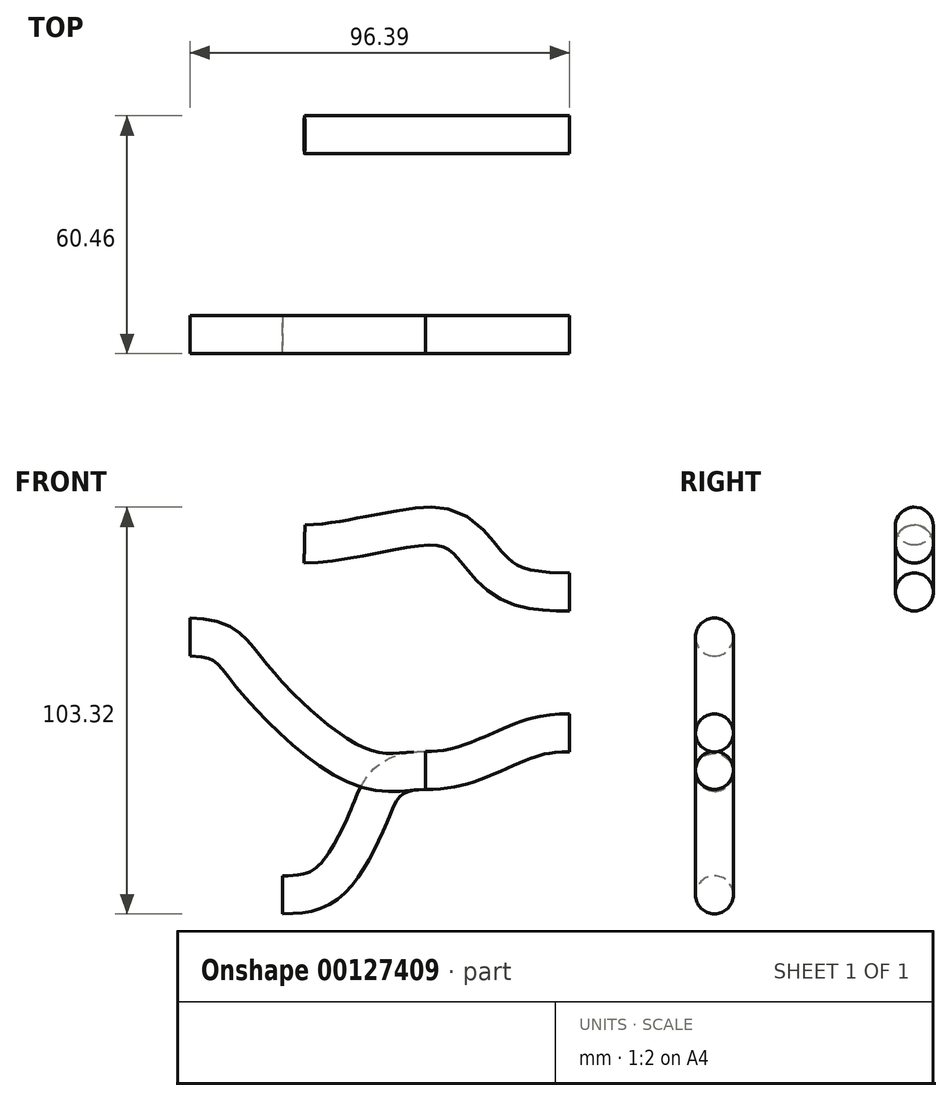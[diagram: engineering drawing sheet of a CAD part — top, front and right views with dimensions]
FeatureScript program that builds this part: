
annotation { "Feature Type Name" : "Feature", "Feature Type Description" : "" }
export const myFeature = defineFeature(function(context is Context, id is Id, definition is map)
    precondition{}
    {
        {
            var Q0;
            Q0=qCreatedBy(makeId("Front.planeOp"),FACE);
            var sketch = newSketch(context, id + "F0", { "sketchPlane" : qUnion([Q0])});
            skFitSpline(sketch, "E0", {"points": [v(-67.31, 32.38) * mm, v(-43.25, 36.06) * mm, v(-28.06, 35.04) * mm, v(-16.85, 23.57) * mm, v(0, 20.22) * mm], "startDerivative": vector(65.29, -0.8) * mm, "endDerivative": vector(70.88, 0.8) * mm});
            skLineSegment(sketch, "E1.bottom", {"start": v(-67.31, 32.38) * mm, "end": v(0, 32.38) * mm});
            skLineSegment(sketch, "E1.top", {"start": v(-67.31, 20.22) * mm, "end": v(0, 20.22) * mm});
            skLineSegment(sketch, "E1.left", {"start": v(-67.31, 32.38) * mm, "end": v(-67.31, 20.22) * mm});
            skLineSegment(sketch, "E1.right", {"start": v(0, 32.38) * mm, "end": v(0, 20.22) * mm});
            skLineSegment(sketch, "E2", {"start": v(-67.31, 32.38) * mm, "end": v(-72.78, 23.64) * mm});
            skLineSegment(sketch, "E3", {"start": v(-72.78, 23.64) * mm, "end": v(-67.31, 20.22) * mm});
            skSolve(sketch);
        }
        {
            var Q0;
            Q0=qCreatedBy(makeId("Front.planeOp"),FACE);
            cPlane(context, id + "F1", {"entities" : qUnion([Q0]), "cplaneType" : CPlaneType.OFFSET, "offset" : 50.8 * mm, "width" : 152.4 * mm, "height" : 152.4 * mm});
        }
        {
            var Q0;
            Q0=qCreatedBy(id+"F1.planeOp",FACE);
            var sketch = newSketch(context, id + "F2", { "sketchPlane" : qUnion([Q0])});
            skLineSegment(sketch, "E4.bottom", {"start": v(-96.4, 8.74) * mm, "end": v(0, 8.74) * mm});
            skLineSegment(sketch, "E4.top", {"start": v(-96.4, -15.6) * mm, "end": v(0, -15.6) * mm});
            skLineSegment(sketch, "E4.left", {"start": v(-96.4, 8.74) * mm, "end": v(-96.4, -15.6) * mm});
            skLineSegment(sketch, "E4.right", {"start": v(0, 8.74) * mm, "end": v(0, -15.6) * mm});
            skLineSegment(sketch, "E5", {"start": v(-96.4, 8.74) * mm, "end": v(-101.2, -14.62) * mm});
            skLineSegment(sketch, "E6", {"start": v(-101.2, -14.62) * mm, "end": v(-96.4, -15.6) * mm});
            skLineSegment(sketch, "E7.top", {"start": v(-96.4, -25.13) * mm, "end": v(0, -25.13) * mm});
            skLineSegment(sketch, "E7.left", {"start": v(-96.4, 8.74) * mm, "end": v(-96.4, -25.13) * mm});
            skLineSegment(sketch, "E7.right", {"start": v(0, 8.74) * mm, "end": v(0, -25.13) * mm});
            skPoint(sketch, "E8", {"position": v(-36.62, -25.13) * mm});
            skFitSpline(sketch, "E9", {"points": [v(0, -15.6) * mm, v(-12.62, -18) * mm, v(-25.44, -23.3) * mm, v(-36.62, -25.13) * mm], "startDerivative": vector(-53.06, 0) * mm, "endDerivative": vector(-43.37, 0) * mm});
            skFitSpline(sketch, "E10", {"points": [v(-36.62, -25.13) * mm, v(-52.77, -24.35) * mm, v(-81.6, 0) * mm, v(-96.4, 8.74) * mm], "startDerivative": vector(-46.79, 0) * mm, "endDerivative": vector(-92.34, 0) * mm});
            skLineSegment(sketch, "E11.bottom", {"start": v(0, -15.6) * mm, "end": v(-72.82, -15.6) * mm});
            skLineSegment(sketch, "E11.top", {"start": v(0, -56.74) * mm, "end": v(-72.82, -56.74) * mm});
            skLineSegment(sketch, "E11.left", {"start": v(0, -15.6) * mm, "end": v(0, -56.74) * mm});
            skLineSegment(sketch, "E11.right", {"start": v(-72.82, -15.6) * mm, "end": v(-72.82, -56.74) * mm});
            skFitSpline(sketch, "E12", {"points": [v(-36.62, -25.13) * mm, v(-50.94, -36.65) * mm, v(-60.86, -53.25) * mm, v(-72.82, -56.74) * mm], "startDerivative": vector(-87.47, 0) * mm, "endDerivative": vector(-55.66, 0) * mm});
            skSolve(sketch);
        }
        {
            var Q0;
            Q0=qCreatedBy(makeId("Right.planeOp"),FACE);
            var sketch = newSketch(context, id + "F3", { "sketchPlane" : qUnion([Q0])});
            skCircle(sketch, "E13", {"center": v(0, 20.22) * mm, "radius": 4.83 * mm});
            skCircle(sketch, "E14", {"center": v(-50.8, -15.6) * mm, "radius": 4.83 * mm});
            skSolve(sketch);
        }
        {
            var Q0;
            Q0=makeQuery(id+"F3.imprint","IMPRINT",FACE,{"disambiguationData":[TD([[makeQuery(id+"F3.imprint","IMPRINT",EDGE,{"derivedFrom":sQuery(id+"F3.wireOp",EDGE,"E13")}),1.0]])]});
            var Q1;
            Q1=sQuery(id+"F0.wireOp",EDGE,"E0");
            sweep(context, id + "F4", {"profiles" : qUnion([Q0]), "path" : qUnion([Q1])});
        }
        {
            var Q0;
            Q0=makeQuery(id+"F3.imprint","IMPRINT",FACE,{"disambiguationData":[TD([[makeQuery(id+"F3.imprint","IMPRINT",EDGE,{"derivedFrom":sQuery(id+"F3.wireOp",EDGE,"E14")}),1.0]])]});
            var Q1;
            Q1=sQuery(id+"F2.wireOp",EDGE,"E9");
            sweep(context, id + "F5", {"profiles" : qUnion([Q0]), "path" : qUnion([Q1])});
        }
        {
            var Q0;
            Q0=makeQuery(id+"F5.opSweep","CAP_FACE",FACE,{"disambiguationData":[OSD([sQuery(id+"F2.wireOp",VERTEX,"E9.end"),sQuery(id+"F3.wireOp",EDGE,"E14")])],"isStart":false});
            var Q1;
            Q1=sQuery(id+"F2.wireOp",EDGE,"E10");
            sweep(context, id + "F6", {"profiles" : qUnion([Q0]), "path" : qUnion([Q1])});
        }
        {
            var Q0;
            Q0=makeQuery(id+"F5.opSweep","CAP_FACE",FACE,{"disambiguationData":[OSD([sQuery(id+"F2.wireOp",VERTEX,"E9.end"),sQuery(id+"F3.wireOp",EDGE,"E14")])],"isStart":false});
            var Q1;
            Q1=sQuery(id+"F2.wireOp",EDGE,"E12");
            sweep(context, id + "F7", {"profiles" : qUnion([Q0]), "path" : qUnion([Q1])});
        }
    });
